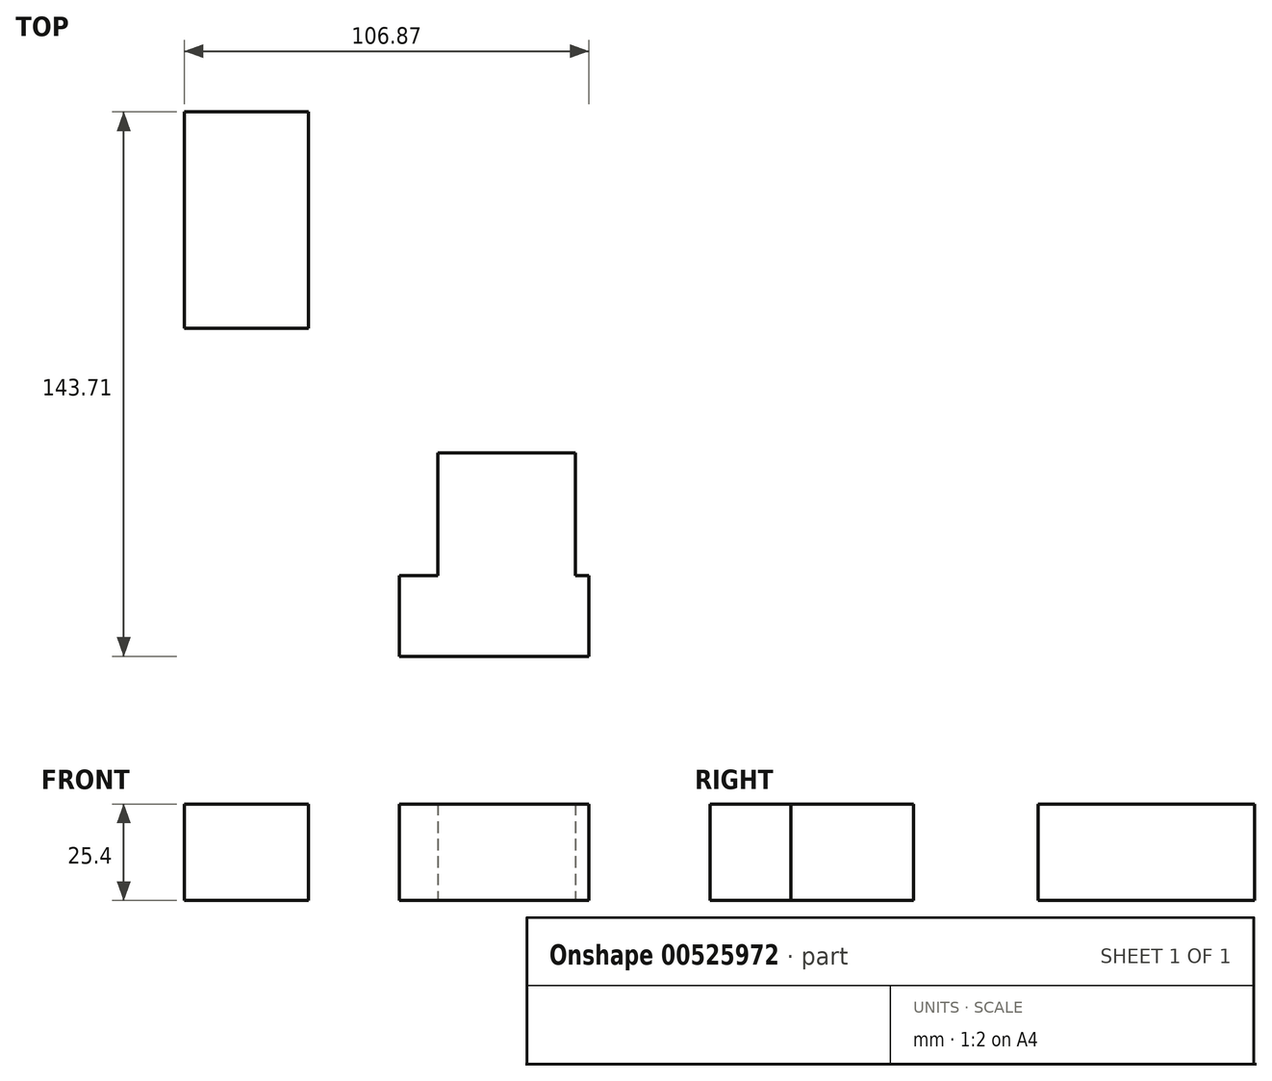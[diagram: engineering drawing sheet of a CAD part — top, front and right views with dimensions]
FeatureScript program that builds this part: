
annotation { "Feature Type Name" : "Feature", "Feature Type Description" : "" }
export const myFeature = defineFeature(function(context is Context, id is Id, definition is map)
    precondition{}
    {
        {
            var Q0;
            Q0=qCreatedBy(makeId("Top.planeOp"),FACE);
            var sketch = newSketch(context, id + "F0", { "sketchPlane" : qUnion([Q0])});
            skLineSegment(sketch, "E0.bottom", {"start": v(-66.96, 191.12) * mm, "end": v(-34.2, 191.12) * mm});
            skLineSegment(sketch, "E0.top", {"start": v(-66.96, 134) * mm, "end": v(-34.2, 134) * mm});
            skLineSegment(sketch, "E0.left", {"start": v(-66.96, 191.12) * mm, "end": v(-66.96, 134) * mm});
            skLineSegment(sketch, "E0.right", {"start": v(-34.2, 191.12) * mm, "end": v(-34.2, 134) * mm});
            skLineSegment(sketch, "E1.bottom", {"start": v(36.25, 49.36) * mm, "end": v(0, 49.36) * mm});
            skLineSegment(sketch, "E1.top", {"start": v(36.25, 101.07) * mm, "end": v(0, 101.07) * mm});
            skLineSegment(sketch, "E1.left", {"start": v(36.25, 49.36) * mm, "end": v(36.25, 101.07) * mm});
            skLineSegment(sketch, "E1.right", {"start": v(0, 49.36) * mm, "end": v(0, 101.07) * mm});
            skLineSegment(sketch, "E2.bottom", {"start": v(-24.74, 134) * mm, "end": v(-34.2, 134) * mm});
            skLineSegment(sketch, "E2.top", {"start": v(-24.74, 134) * mm, "end": v(-34.2, 134) * mm});
            skLineSegment(sketch, "E2.left", {"start": v(-24.74, 134) * mm, "end": v(-24.74, 134) * mm});
            skLineSegment(sketch, "E2.right", {"start": v(-34.2, 134) * mm, "end": v(-34.2, 134) * mm});
            skLineSegment(sketch, "E3.bottom", {"start": v(39.9, 47.41) * mm, "end": v(-10.16, 47.41) * mm});
            skLineSegment(sketch, "E3.top", {"start": v(39.9, 68.67) * mm, "end": v(-10.16, 68.67) * mm});
            skLineSegment(sketch, "E3.left", {"start": v(39.9, 47.41) * mm, "end": v(39.9, 68.67) * mm});
            skLineSegment(sketch, "E3.right", {"start": v(-10.16, 47.41) * mm, "end": v(-10.16, 68.67) * mm});
            skSolve(sketch);
        }
        {
            var Q0;
            Q0 = qSketchRegion(id + "F0", true);
            extrude(context, id + "F1", {"entities" : qUnion([Q0]), "depth" : 25.4 * mm, "offsetDistance" : 25.4 * mm});
        }
    });
